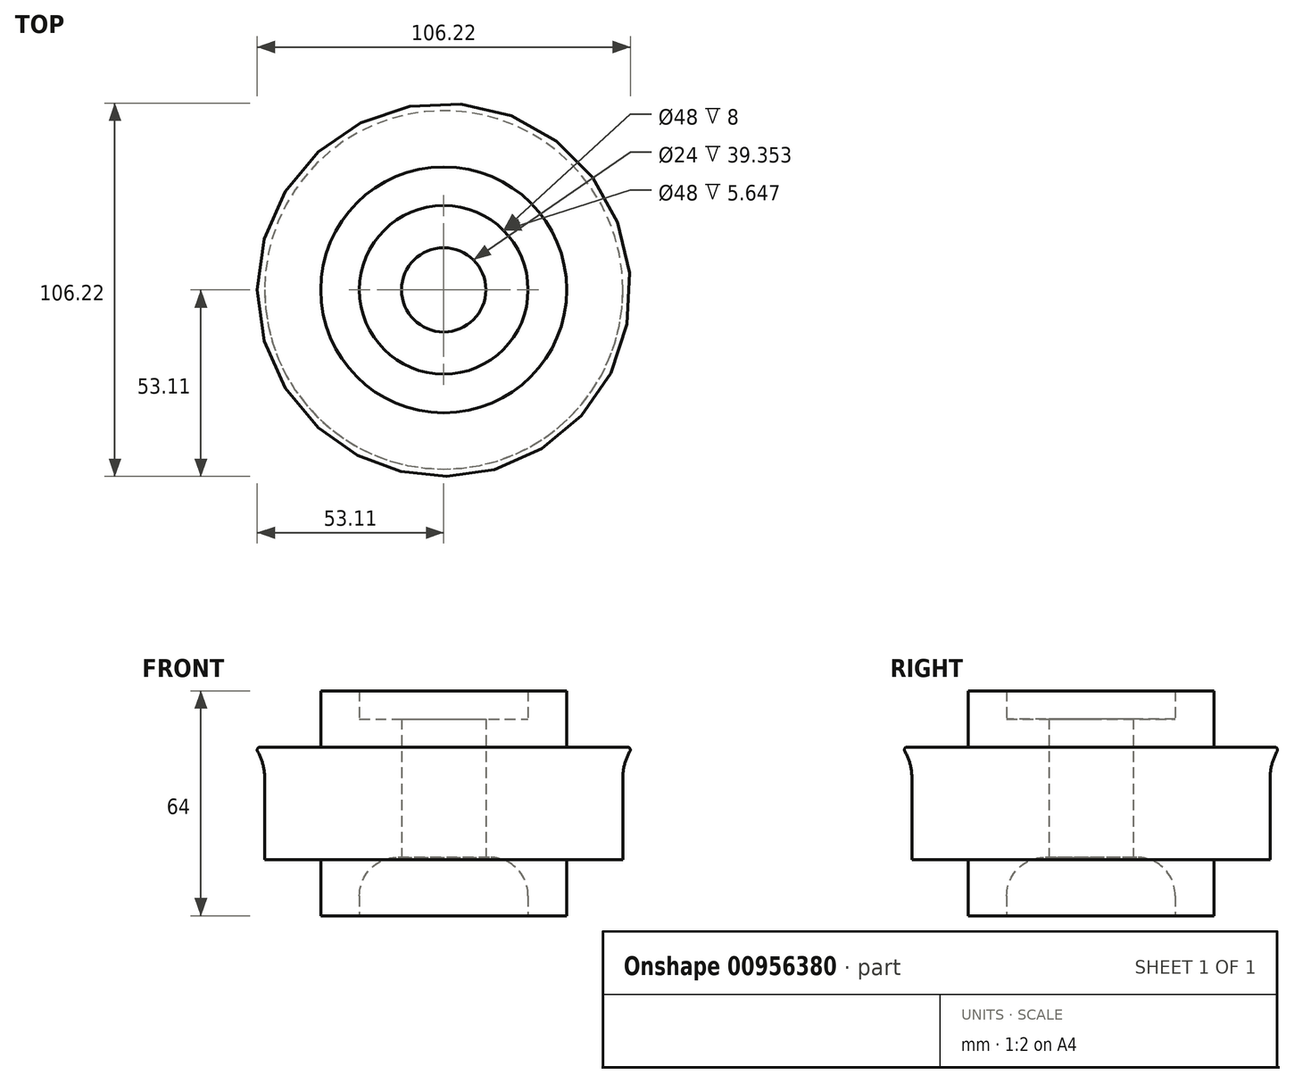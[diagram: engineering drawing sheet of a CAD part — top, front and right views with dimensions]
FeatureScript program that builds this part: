
annotation { "Feature Type Name" : "Feature", "Feature Type Description" : "" }
export const myFeature = defineFeature(function(context is Context, id is Id, definition is map)
    precondition{}
    {
        {
            var Q0;
            Q0=qCreatedBy(makeId("Front.planeOp"),FACE);
            var sketch = newSketch(context, id + "F0", { "sketchPlane" : qUnion([Q0])});
            skLineSegment(sketch, "E0", {"start": v(0, 0) * mm, "end": v(0, 96.09) * mm, "construction": true});
            skLineSegment(sketch, "E1", {"start": v(24, 77.49) * mm, "end": v(24, 85.49) * mm});
            skLineSegment(sketch, "E2", {"start": v(24, 85.49) * mm, "end": v(35, 85.49) * mm});
            skLineSegment(sketch, "E3", {"start": v(35, 85.49) * mm, "end": v(35, 69.49) * mm});
            skLineSegment(sketch, "E4", {"start": v(35, 69.49) * mm, "end": v(51, 69.49) * mm});
            skLineSegment(sketch, "E5", {"start": v(51, 69.49) * mm, "end": v(51, 37.49) * mm});
            skLineSegment(sketch, "E6", {"start": v(51, 37.49) * mm, "end": v(35, 37.49) * mm});
            skLineSegment(sketch, "E7", {"start": v(35, 37.49) * mm, "end": v(35, 21.49) * mm});
            skLineSegment(sketch, "E8", {"start": v(35, 21.49) * mm, "end": v(24, 21.49) * mm});
            skLineSegment(sketch, "E9", {"start": v(24, 21.49) * mm, "end": v(24, 38.14) * mm});
            skLineSegment(sketch, "E10", {"start": v(12, 38.14) * mm, "end": v(12, 77.49) * mm});
            skLineSegment(sketch, "E11", {"start": v(24, 38.14) * mm, "end": v(12, 38.14) * mm});
            skLineSegment(sketch, "E12", {"start": v(24, 77.49) * mm, "end": v(12, 77.49) * mm});
            skLineSegment(sketch, "E13", {"start": v(51, 69.49) * mm, "end": v(53.77, 69.49) * mm});
            skLineSegment(sketch, "E14", {"start": v(53.77, 69.49) * mm, "end": v(51, 65.6) * mm});
            skSolve(sketch);
        }
        {
            var Q0;
            Q0 = qSketchRegion(id + "F0", true);
            var Q1;
            Q1=sQuery(id+"F0.wireOp",EDGE,"E0");
            revolve(context, id + "F1", {"surfaceOperationType" : NewSurfaceOperationType.NEW, "entities" : qUnion([Q0]), "axis" : qUnion([Q1]), "revolveType" : RevolveType.FULL});
        }
        {
            var Q0;
            Q0=makeQuery(id+"F1.opRevolve","SWEPT_EDGE",EDGE,{"disambiguationData":[OSD([sQuery(id+"F0.wireOp",EDGE,"E9"),sQuery(id+"F0.wireOp",EDGE,"E11")])]});
            fillet(context, id + "F2", {"entities" : qUnion([Q0]), "tangentPropagation" : true, "radius" : 11 * mm, "defaultsChanged" : true, "vertexSettings" : [], "allowEdgeOverflow" : false});
        }
        {
            var Q0;
            Q0=makeQuery(id+"F1.opRevolve","SWEPT_EDGE",EDGE,{"disambiguationData":[OSD([sQuery(id+"F0.wireOp",EDGE,"E5"),sQuery(id+"F0.wireOp",EDGE,"E14")])]});
            fillet(context, id + "F3", {"entities" : qUnion([Q0]), "tangentPropagation" : true, "radius" : 15 * mm, "defaultsChanged" : true, "vertexSettings" : [], "allowEdgeOverflow" : false});
        }
        {
            var Q0;
            Q0=makeQuery(id+"F3.opFillet","BLEND_EDGE",EDGE,{"blendedFrom":[makeQuery(id+"F1.opRevolve","SWEPT_EDGE",EDGE,{"disambiguationData":[OSD([sQuery(id+"F0.wireOp",EDGE,"E5"),sQuery(id+"F0.wireOp",EDGE,"E14")])]}),makeQuery(id+"F1.opRevolve","SWEPT_FACE",FACE,{"disambiguationData":[OSD([sQuery(id+"F0.wireOp",EDGE,"E4"),sQuery(id+"F0.wireOp",EDGE,"E13")])]})],"blendedInto":[makeQuery(id+"F1.opRevolve","SWEPT_FACE",FACE,{"disambiguationData":[OSD([sQuery(id+"F0.wireOp",EDGE,"E4"),sQuery(id+"F0.wireOp",EDGE,"E13")])]})]});
            fillet(context, id + "F4", {"entities" : qUnion([Q0]), "tangentPropagation" : true, "radius" : 0.8 * mm, "defaultsChanged" : true, "vertexSettings" : [], "allowEdgeOverflow" : false});
        }
    });
